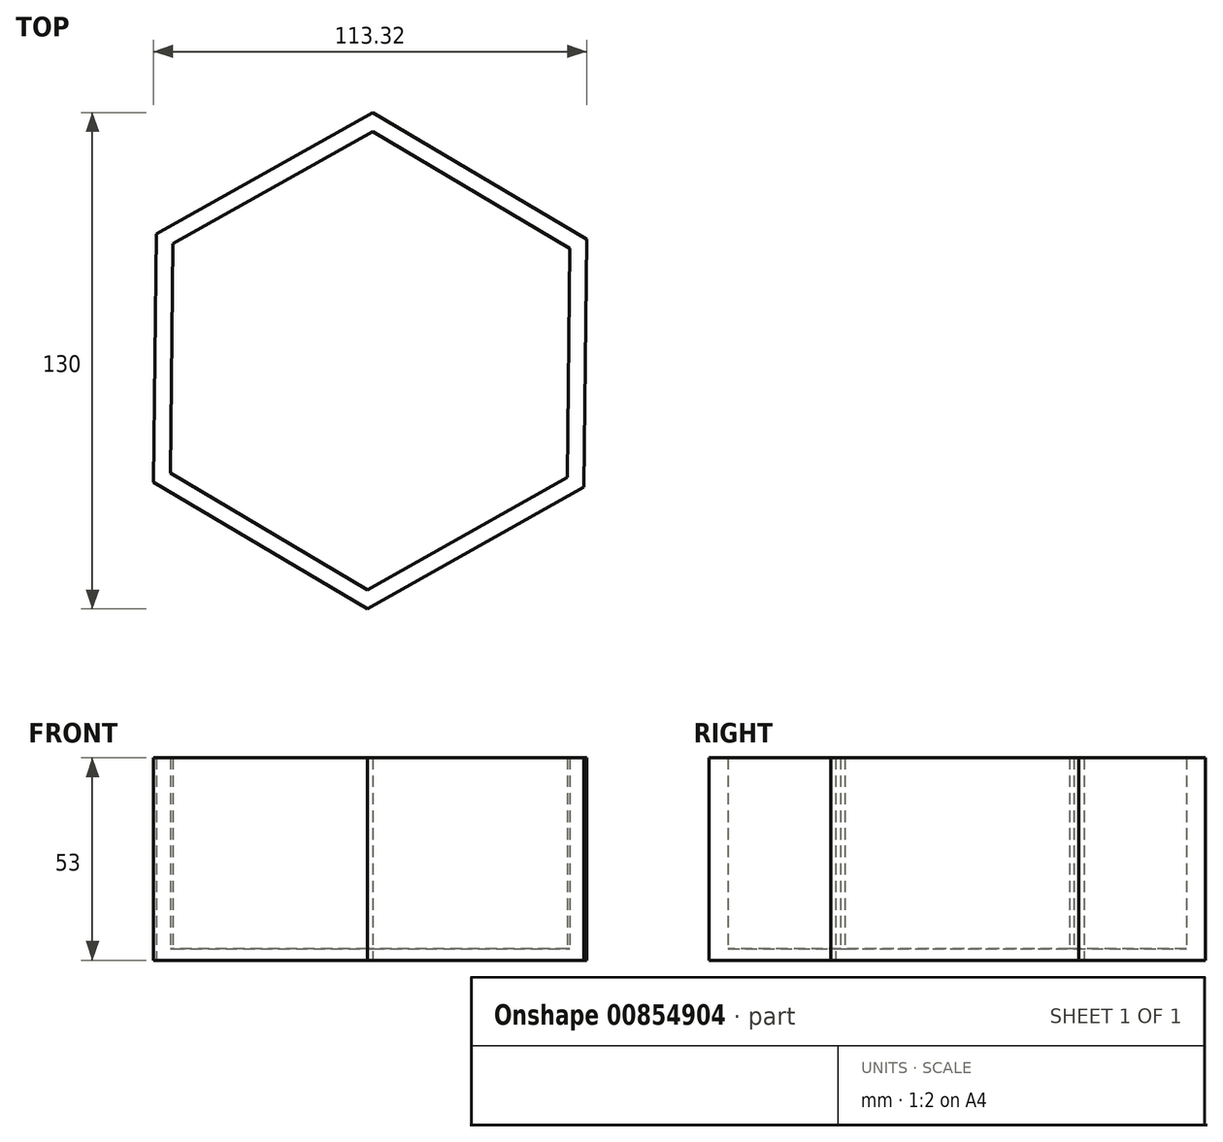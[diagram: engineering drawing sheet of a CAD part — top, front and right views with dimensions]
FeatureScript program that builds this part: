
annotation { "Feature Type Name" : "Feature", "Feature Type Description" : "" }
export const myFeature = defineFeature(function(context is Context, id is Id, definition is map)
    precondition{}
    {
        {
            var Q0;
            Q0=qCreatedBy(makeId("Top.planeOp"),FACE);
            var sketch = newSketch(context, id + "F0", { "sketchPlane" : qUnion([Q0])});
            skCircle(sketch, "E0.cCircle", {"center": v(0, 0) * mm, "radius": 51.96 * mm, "construction": true});
            skLineSegment(sketch, "E0.0", {"start": v(-0.69, -60) * mm, "end": v(-52.3, -29.4) * mm});
            skLineSegment(sketch, "E0.1", {"start": v(-52.3, -29.4) * mm, "end": v(-51.61, 30.6) * mm});
            skLineSegment(sketch, "E0.2", {"start": v(-51.61, 30.6) * mm, "end": v(0.69, 60) * mm});
            skLineSegment(sketch, "E0.3", {"start": v(0.69, 60) * mm, "end": v(52.3, 29.4) * mm});
            skLineSegment(sketch, "E0.4", {"start": v(52.3, 29.4) * mm, "end": v(51.61, -30.6) * mm});
            skLineSegment(sketch, "E0.5", {"start": v(51.61, -30.6) * mm, "end": v(-0.69, -60) * mm});
            skPoint(sketch, "E0.0.midPoint", {"position": v(-26.5, -44.7) * mm});
            skCircle(sketch, "E1.cCircle", {"center": v(0, 0) * mm, "radius": 56.3 * mm, "construction": true});
            skLineSegment(sketch, "E1.0", {"start": v(-56.66, -31.85) * mm, "end": v(-55.91, 33.14) * mm});
            skLineSegment(sketch, "E1.1", {"start": v(-55.91, 33.14) * mm, "end": v(0.75, 65) * mm});
            skLineSegment(sketch, "E1.2", {"start": v(0.75, 65) * mm, "end": v(56.66, 31.85) * mm});
            skLineSegment(sketch, "E1.3", {"start": v(56.66, 31.85) * mm, "end": v(55.91, -33.14) * mm});
            skLineSegment(sketch, "E1.4", {"start": v(55.91, -33.14) * mm, "end": v(-0.75, -65) * mm});
            skLineSegment(sketch, "E1.5", {"start": v(-0.75, -65) * mm, "end": v(-56.66, -31.85) * mm});
            skPoint(sketch, "E1.0.midPoint", {"position": v(-56.29, 0.65) * mm});
            skSolve(sketch);
        }
        {
            var Q0;
            Q0 = qSketchRegion(id + "F0", true);
            extrude(context, id + "F1", {"entities" : qUnion([Q0]), "depth" : 50 * mm, "offsetDistance" : 25 * mm});
        }
        {
            var Q0;
            Q0=makeQuery(id+"F0.imprint","IMPRINT",FACE,{"disambiguationData":[TD([[makeQuery(id+"F0.imprint","IMPRINT",EDGE,{"derivedFrom":sQuery(id+"F0.wireOp",EDGE,"E0.0")}),-1.0]])]});
            var Q1;
            Q1=makeQuery(id+"F0.imprint","IMPRINT",FACE,{"disambiguationData":[TD([[makeQuery(id+"F0.imprint","IMPRINT",EDGE,{"derivedFrom":sQuery(id+"F0.wireOp",EDGE,"E0.0")}),1.0]])]});
            extrude(context, id + "F2", {"entities" : qUnion([Q0, Q1]), "operationType" : NewBodyOperationType.ADD, "oppositeDirection" : true, "depth" : 3 * mm, "offsetDistance" : 25 * mm});
        }
    });
